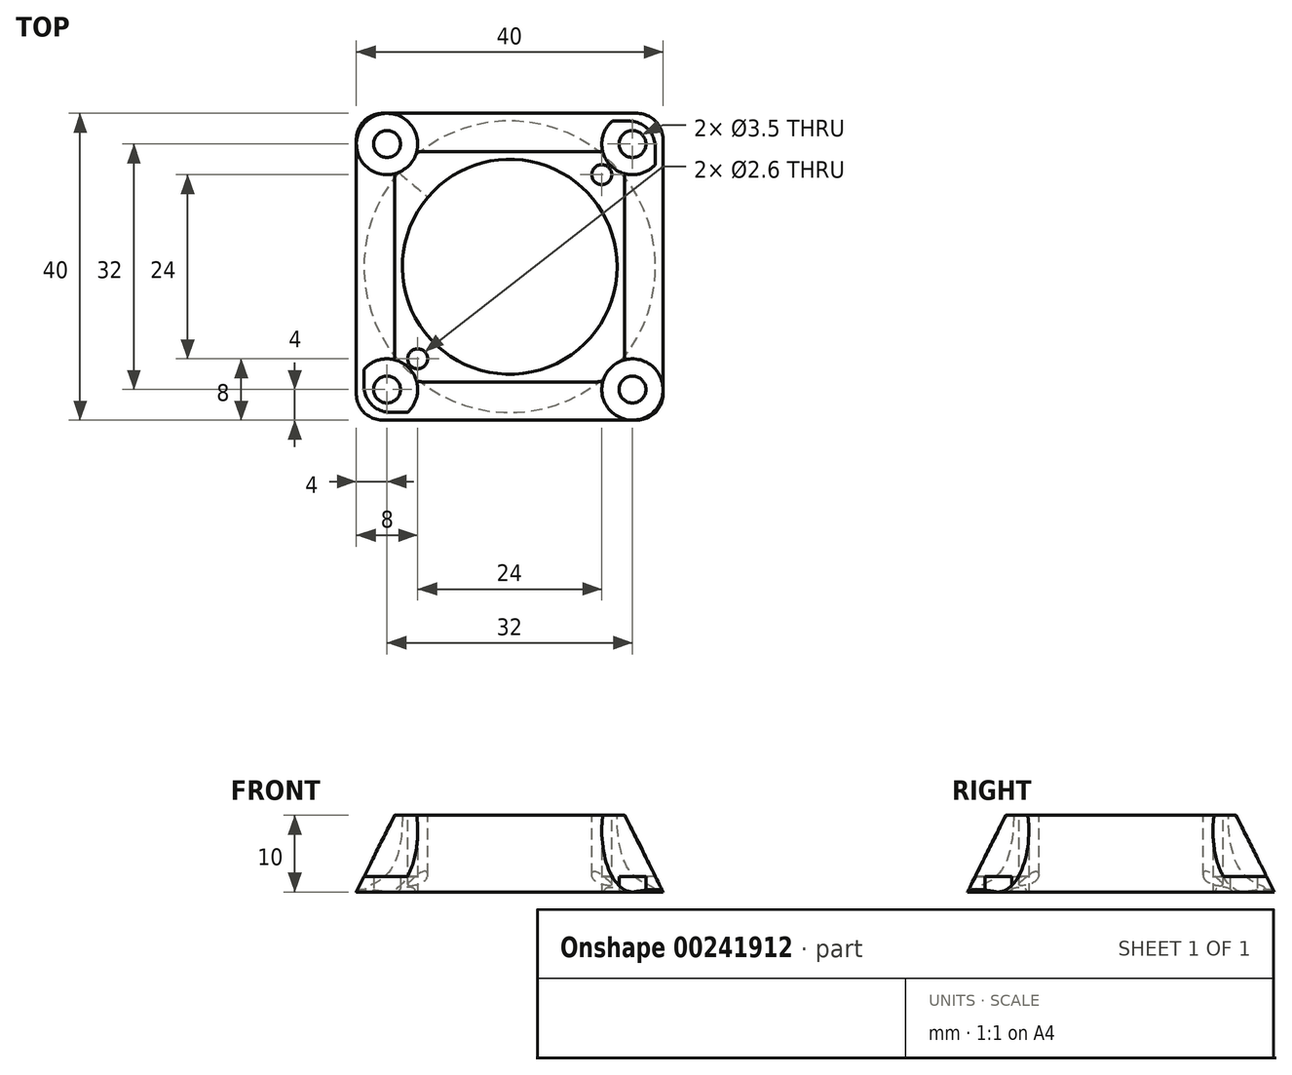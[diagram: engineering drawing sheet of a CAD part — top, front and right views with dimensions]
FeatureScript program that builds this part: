
annotation { "Feature Type Name" : "Feature", "Feature Type Description" : "" }
export const myFeature = defineFeature(function(context is Context, id is Id, definition is map)
    precondition{}
    {
        {
            var Q0;
            Q0=qCreatedBy(makeId("Top.planeOp"),FACE);
            var sketch = newSketch(context, id + "F0", { "sketchPlane" : qUnion([Q0])});
            skLineSegment(sketch, "E0.bottom", {"start": v(20, -20) * mm, "end": v(-20, -20) * mm});
            skLineSegment(sketch, "E0.top", {"start": v(20, 20) * mm, "end": v(-20, 20) * mm});
            skLineSegment(sketch, "E0.left", {"start": v(20, -20) * mm, "end": v(20, 20) * mm});
            skLineSegment(sketch, "E0.right", {"start": v(-20, -20) * mm, "end": v(-20, 20) * mm});
            skPoint(sketch, "E0.middle", {"position": v(0, 0) * mm});
            skCircle(sketch, "E1", {"center": v(-16, -16) * mm, "radius": 1.75 * mm});
            skCircle(sketch, "E2", {"center": v(-16, -16) * mm, "radius": 4 * mm});
            skCircle(sketch, "E3.MirrorC", {"center": v(-16, 16) * mm, "radius": 4 * mm});
            skCircle(sketch, "E4.MirrorC", {"center": v(-16, 16) * mm, "radius": 1.75 * mm});
            skCircle(sketch, "E5.MirrorC", {"center": v(16, 16) * mm, "radius": 1.75 * mm});
            skCircle(sketch, "E6.MirrorC", {"center": v(16, 16) * mm, "radius": 4 * mm});
            skCircle(sketch, "E7.MirrorC", {"center": v(16, -16) * mm, "radius": 1.75 * mm});
            skCircle(sketch, "E8.MirrorC", {"center": v(16, -16) * mm, "radius": 4 * mm});
            skSolve(sketch);
        }
        {
            var Q0;
            Q0=qCreatedBy(makeId("Top.planeOp"),FACE);
            var sketch = newSketch(context, id + "F1", { "sketchPlane" : qUnion([Q0])});
            skLineSegment(sketch, "E9.bottom", {"start": v(20, 20) * mm, "end": v(-20, 20) * mm});
            skLineSegment(sketch, "E9.top", {"start": v(20, -20) * mm, "end": v(-20, -20) * mm});
            skLineSegment(sketch, "E9.left", {"start": v(20, 20) * mm, "end": v(20, -20) * mm});
            skLineSegment(sketch, "E9.right", {"start": v(-20, 20) * mm, "end": v(-20, -20) * mm});
            skPoint(sketch, "E9.middle", {"position": v(0, 0) * mm});
            skSolve(sketch);
        }
        {
            var Q0;
            Q0=qCreatedBy(makeId("Top.planeOp"),FACE);
            var sketch = newSketch(context, id + "F2", { "sketchPlane" : qUnion([Q0])});
            skCircle(sketch, "E10", {"center": v(0, 0) * mm, "radius": 19 * mm});
            skSolve(sketch);
        }
        {
            var Q0;
            Q0=qCreatedBy(makeId("Top.planeOp"),FACE);
            cPlane(context, id + "F3", {"entities" : qUnion([Q0]), "cplaneType" : CPlaneType.OFFSET, "offset" : 10 * mm, "width" : 150 * mm, "height" : 150 * mm});
        }
        {
            var Q0;
            Q0=qCreatedBy(id+"F3.planeOp",FACE);
            var sketch = newSketch(context, id + "F4", { "sketchPlane" : qUnion([Q0])});
            skLineSegment(sketch, "E11", {"start": v(0, 29.99) * mm, "end": v(0, -8.53) * mm, "construction": true});
            skLineSegment(sketch, "E12", {"start": v(26.67, 0) * mm, "end": v(-7.39, 0) * mm, "construction": true});
            skCircle(sketch, "E13", {"center": v(12, 12) * mm, "radius": 1.3 * mm});
            skCircle(sketch, "E14.MirrorC", {"center": v(-12, 12) * mm, "radius": 1.3 * mm});
            skCircle(sketch, "E15.MirrorC", {"center": v(12, -12) * mm, "radius": 1.3 * mm});
            skCircle(sketch, "E16.MirrorC", {"center": v(-12, -12) * mm, "radius": 1.3 * mm});
            skPoint(sketch, "E17", {"position": v(0, 0) * mm});
            skSolve(sketch);
        }
        {
            var Q0;
            Q0=qCreatedBy(id+"F3.planeOp",FACE);
            var sketch = newSketch(context, id + "F5", { "sketchPlane" : qUnion([Q0])});
            skPoint(sketch, "E18.0", {"position": v(0, 0) * mm});
            skLineSegment(sketch, "E19.bottom", {"start": v(15, -15) * mm, "end": v(-15, -15) * mm});
            skLineSegment(sketch, "E19.top", {"start": v(15, 15) * mm, "end": v(-15, 15) * mm});
            skLineSegment(sketch, "E19.left", {"start": v(15, -15) * mm, "end": v(15, 15) * mm});
            skLineSegment(sketch, "E19.right", {"start": v(-15, -15) * mm, "end": v(-15, 15) * mm});
            skSolve(sketch);
        }
        {
            var Q0;
            Q0=qCreatedBy(id+"F3.planeOp",FACE);
            var sketch = newSketch(context, id + "F6", { "sketchPlane" : qUnion([Q0])});
            skPoint(sketch, "E20.0", {"position": v(0, 0) * mm});
            skCircle(sketch, "E21", {"center": v(0, 0) * mm, "radius": 14 * mm});
            skSolve(sketch);
        }
        {
            var Q0;
            Q0=makeQuery(id+"F1.imprint","IMPRINT",FACE,{"disambiguationData":[TD([[makeQuery(id+"F1.imprint","IMPRINT",EDGE,{"derivedFrom":sQuery(id+"F1.wireOp",EDGE,"E9.bottom")}),1.0]])]});
            var Q1;
            Q1=makeQuery(id+"F5.imprint","IMPRINT",FACE,{"disambiguationData":[TD([[makeQuery(id+"F5.imprint","IMPRINT",EDGE,{"derivedFrom":sQuery(id+"F5.wireOp",EDGE,"E19.bottom")}),-1.0]])]});
            loft(context, id + "F7", {"sheetProfilesArray" : [{ "sheetProfileEntities" : qUnion([Q0]) }, { "sheetProfileEntities" : qUnion([Q1]) }]});
        }
        {
            var Q1;
            Q1=makeQuery(id+"F2.imprint","IMPRINT",FACE,{"disambiguationData":[TD([[makeQuery(id+"F2.imprint","IMPRINT",EDGE,{"derivedFrom":sQuery(id+"F2.wireOp",EDGE,"E10")}),1.0]])]});
            var Q2;
            Q2=makeQuery(id+"F6.imprint","IMPRINT",FACE,{"disambiguationData":[TD([[makeQuery(id+"F6.imprint","IMPRINT",EDGE,{"derivedFrom":sQuery(id+"F6.wireOp",EDGE,"E21")}),1.0]])]});
            loft(context, id + "F8", {"operationType" : NewBodyOperationType.REMOVE, "startCondition" : LoftEndDerivativeType.NORMAL_TO_PROFILE, "startMagnitude" : 0.5, "endCondition" : LoftEndDerivativeType.NORMAL_TO_PROFILE, "endMagnitude" : 3, "sheetProfilesArray" : [{ "sheetProfileEntities" : qUnion([Q1]) }, { "sheetProfileEntities" : qUnion([Q2]) }]});
        }
        {
            var Q0;
            Q0=makeQuery(id+"F7.opLoft","SWEPT_EDGE",EDGE,{"disambiguationData":[OSD([sQuery(id+"F1.wireOp",EDGE,"E9.bottom"),sQuery(id+"F1.wireOp",EDGE,"E9.left"),sQuery(id+"F5.wireOp",EDGE,"E19.top"),sQuery(id+"F5.wireOp",EDGE,"E19.left")])]});
            var Q1;
            Q1=makeQuery(id+"F7.opLoft","SWEPT_EDGE",EDGE,{"disambiguationData":[OSD([sQuery(id+"F1.wireOp",EDGE,"E9.top"),sQuery(id+"F1.wireOp",EDGE,"E9.left"),sQuery(id+"F5.wireOp",EDGE,"E19.bottom"),sQuery(id+"F5.wireOp",EDGE,"E19.left")])]});
            var Q2;
            Q2=makeQuery(id+"F7.opLoft","SWEPT_EDGE",EDGE,{"disambiguationData":[OSD([sQuery(id+"F1.wireOp",EDGE,"E9.bottom"),sQuery(id+"F1.wireOp",EDGE,"E9.right"),sQuery(id+"F5.wireOp",EDGE,"E19.top"),sQuery(id+"F5.wireOp",EDGE,"E19.right")])]});
            var Q3;
            Q3=makeQuery(id+"F7.opLoft","SWEPT_EDGE",EDGE,{"disambiguationData":[OSD([sQuery(id+"F1.wireOp",EDGE,"E9.top"),sQuery(id+"F1.wireOp",EDGE,"E9.right"),sQuery(id+"F5.wireOp",EDGE,"E19.bottom"),sQuery(id+"F5.wireOp",EDGE,"E19.right")])]});
            fillet(context, id + "F9", {"entities" : qUnion([Q0, Q1, Q2, Q3]), "radius" : 4 * mm, "tangentPropagation" : true, "allowEdgeOverflow" : false});
        }
        {
            var Q0;
            Q0=makeQuery(id+"F4.imprint","IMPRINT",FACE,{"disambiguationData":[TD([[makeQuery(id+"F4.imprint","IMPRINT",EDGE,{"derivedFrom":sQuery(id+"F4.wireOp",EDGE,"E14.MirrorC")}),-1.0]])]});
            var Q1;
            Q1=makeQuery(id+"F4.imprint","IMPRINT",FACE,{"disambiguationData":[TD([[makeQuery(id+"F4.imprint","IMPRINT",EDGE,{"derivedFrom":sQuery(id+"F4.wireOp",EDGE,"E13")}),1.0]])]});
            var Q2;
            Q2=makeQuery(id+"F4.imprint","IMPRINT",FACE,{"disambiguationData":[TD([[makeQuery(id+"F4.imprint","IMPRINT",EDGE,{"derivedFrom":sQuery(id+"F4.wireOp",EDGE,"E15.MirrorC")}),-1.0]])]});
            var Q3;
            Q3=makeQuery(id+"F4.imprint","IMPRINT",FACE,{"disambiguationData":[TD([[makeQuery(id+"F4.imprint","IMPRINT",EDGE,{"derivedFrom":sQuery(id+"F4.wireOp",EDGE,"E16.MirrorC")}),1.0]])]});
            extrude(context, id + "F10", {"entities" : qUnion([Q0, Q1, Q2, Q3]), "operationType" : NewBodyOperationType.REMOVE, "oppositeDirection" : true, "depth" : 15 * mm});
        }
        {
            var Q0;
            Q0=makeQuery(id+"F0.imprint","IMPRINT",FACE,{"disambiguationData":[TD([[makeQuery(id+"F0.imprint","IMPRINT",EDGE,{"derivedFrom":sQuery(id+"F0.wireOp",EDGE,"E4.MirrorC")}),-1.0]])]});
            var Q1;
            Q1=makeQuery(id+"F0.imprint","IMPRINT",FACE,{"disambiguationData":[TD([[makeQuery(id+"F0.imprint","IMPRINT",EDGE,{"derivedFrom":sQuery(id+"F0.wireOp",EDGE,"E7.MirrorC")}),-1.0]])]});
            var Q2;
            Q2=makeQuery(id+"F0.imprint","IMPRINT",FACE,{"disambiguationData":[TD([[makeQuery(id+"F0.imprint","IMPRINT",EDGE,{"derivedFrom":sQuery(id+"F0.wireOp",EDGE,"E1")}),1.0]])]});
            var Q3;
            Q3=makeQuery(id+"F0.imprint","IMPRINT",FACE,{"disambiguationData":[TD([[makeQuery(id+"F0.imprint","IMPRINT",EDGE,{"derivedFrom":sQuery(id+"F0.wireOp",EDGE,"E5.MirrorC")}),1.0]])]});
            extrude(context, id + "F11", {"entities" : qUnion([Q0, Q1, Q2, Q3]), "operationType" : NewBodyOperationType.REMOVE, "depth" : 25 * mm});
        }
        {
            var Q0;
            Q0=makeQuery(id+"F0.imprint","IMPRINT",FACE,{"disambiguationData":[TD([[makeQuery(id+"F0.imprint","IMPRINT",EDGE,{"derivedFrom":sQuery(id+"F0.wireOp",EDGE,"E4.MirrorC")}),1.0]])]});
            var Q1;
            Q1=makeQuery(id+"F0.imprint","IMPRINT",FACE,{"disambiguationData":[TD([[makeQuery(id+"F0.imprint","IMPRINT",EDGE,{"derivedFrom":sQuery(id+"F0.wireOp",EDGE,"E7.MirrorC")}),1.0]])]});
            var Q2;
            Q2=makeQuery(id+"F0.imprint","IMPRINT",FACE,{"disambiguationData":[TD([[makeQuery(id+"F0.imprint","IMPRINT",EDGE,{"derivedFrom":sQuery(id+"F0.wireOp",EDGE,"E1")}),-1.0]])]});
            var Q3;
            Q3=makeQuery(id+"F0.imprint","IMPRINT",FACE,{"disambiguationData":[TD([[makeQuery(id+"F0.imprint","IMPRINT",EDGE,{"derivedFrom":sQuery(id+"F0.wireOp",EDGE,"E5.MirrorC")}),-1.0]])]});
            extrude(context, id + "F12", {"entities" : qUnion([Q0, Q1, Q2, Q3]), "operationType" : NewBodyOperationType.REMOVE, "depth" : 25 * mm, "hasSecondDirection" : true, "secondDirectionOppositeDirection" : false, "secondDirectionDepth" : 2 * mm});
        }
    });
